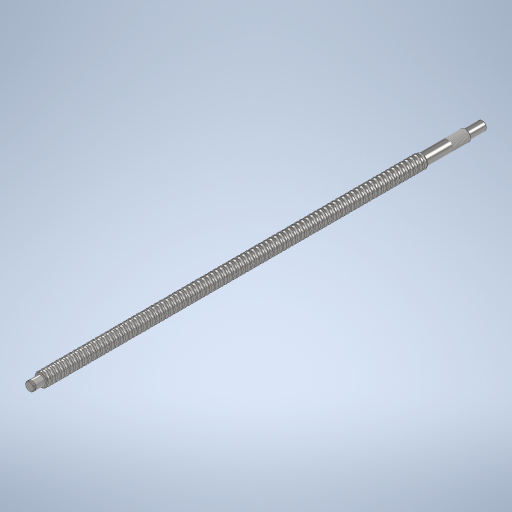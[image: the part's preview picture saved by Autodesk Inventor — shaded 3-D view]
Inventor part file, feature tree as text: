
AUTODESK INVENTOR PART (.ipt)
format: ipt  version: 2024 (Build 280153000, 153)  size: 530,944 bytes
history: native  units: mm
features: sketch x7, extrude x5, plane x2, projected_geometry x2, thread x1, chamfer x1, helix x1
ambient origin geometry x8: Origin, YZ Plane, XZ Plane, XY Plane, X Axis, Y Axis, Z Axis, Center Point
bodies: Solid1 (feature_tree)
feature tree (19):
  extrude  "Extrusion1"  Depth=15.0mm TaperAngle=0.0deg
  extrude  "Extrusion2"  Depth=10.0mm TaperAngle=0.0deg
  sketch  "Sketch3"  dims[d6=-400.0mm d7=8.0mm]
  plane  "Work Plane1"
  extrude  "Extrusion3"  Depth=8.0mm
  extrude  "Extrusion4"  Depth=10.0mm
  plane  "Work Plane2"
  extrude  "Extrusion5"  Depth=10.0mm
  thread  "Thread1"  [1 undecoded]
  chamfer  "Chamfer1"  Distance=0.9mm
  helix  "Coil1"  [1 undecoded]
  sketch  "Sketch1"  dims[d0=8.0mm d1=15.0mm d2=0.0mm]
  sketch  "Sketch2"  dims[d3=10.0mm d4=39.0mm d5=0.0mm]
  sketch  "Sketch4"  dims[d8=10.0mm d9=0.0mm d10=12.0mm]
  sketch  "Sketch5"  dims[d11=10.0mm d12=0.0mm d13=7.9mm d14=7.6mm d15=0.9mm d16=0.0mm d17=16.0mm d18=0.0mm]
  sketch  "Sketch6"  dims[d19=0.5mm d20=2.0mm d21=45.0deg]
  sketch  "Sketch7"  dims[d22=3.0mm d23=1.75mm d24=4.0mm d25=400.0mm d26=2.5mm d27=0.0mm d28=90.0deg d29=90.0deg d30=0.0mm d31=0.0mm]
  projected_geometry  "Project Cut Edges1"
  projected_geometry  "Project Cut Edges2"
note: 2 required parameter values undecoded (feature->parameter linkage not recoverable at this tier; creation-order binding heuristic only, values carry confidence <= 0.55)
